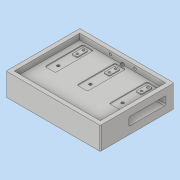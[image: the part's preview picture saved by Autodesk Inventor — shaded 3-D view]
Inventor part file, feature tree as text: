
AUTODESK INVENTOR PART (.ipt)
format: ipt  version: 2018 (Build 220112000, 112)  size: 459,264 bytes
history: native  units: mm
features: sketch x15, projected_geometry x14, extrude x8, hole x7, fillet x4, plane x1, mirror x1
ambient origin geometry x8: Origin, YZ Plane, XZ Plane, XY Plane, X Axis, Y Axis, Z Axis, Center Point
bodies: Volumenkörper1 (feature_tree)
feature tree (50):
  extrude  "Extrusion1"  Depth=180.0mm
  extrude  "Extrusion2"  Depth=10.0mm
  extrude  "Extrusion3"  Depth=27.0mm
  hole  "Bohrung1"  [1 undecoded]
  extrude  "Extrusion4"  Depth=20.0mm
  extrude  "Extrusion5"  Depth=65.5mm
  hole  "Bohrung2"  [1 undecoded]
  hole  "Bohrung3"  [1 undecoded]
  hole  "Bohrung4"  [1 undecoded]
  hole  "Bohrung5"  [1 undecoded]
  extrude  "Extrusion6"  Depth=2.0mm
  extrude  "Extrusion7"  Depth=6.5mm
  fillet  "Rundung3"  Radius=6.5mm
  plane  "Arbeitsebene1"
  mirror  "Spiegeln1"
  hole  "Bohrung6"  [1 undecoded]
  extrude  "Extrusion8"  Depth=6.5mm
  hole  "Bohrung7"  [1 undecoded]
  fillet  "Rundung2"  Radius=93.0mm
  fillet  "Rundung1"  Radius=93.0mm
  fillet  "Rundung4"  Radius=3.5mm
  sketch  "Skizze1"  dims[d0=230.0mm d1=180.0mm]
  sketch  "Skizze2"  dims[d2=39.0mm d3=0.0mm d4=10.0mm]
  projected_geometry  "Projizierte Kontur1"
  sketch  "Skizze3"  dims[d5=16.0mm d6=0.0mm d7=27.0mm]
  sketch  "Skizze4"  dims[d8=13.0mm d9=27.0mm d10=13.0mm]
  projected_geometry  "Projizierte Kontur2"
  projected_geometry  "Projizierte Kontur3"
  projected_geometry  "Projizierte Kontur4"
  projected_geometry  "Projizierte Kontur5"
  sketch  "Skizze5"  dims[d11=27.0mm d12=13.0mm d13=20.0mm]
  projected_geometry  "Projizierte Kontur6"
  sketch  "Skizze6"  dims[d14=20.0mm d15=65.5mm]
  projected_geometry  "Projizierte Kontur7"
  sketch  "Skizze7"  dims[d16=65.5mm d17=12.5mm]
  projected_geometry  "Projizierte Kontur8"
  sketch  "Skizze8"  dims[d18=2.0mm d19=0.0mm d20=15.0mm]
  projected_geometry  "Projizierte Kontur9"
  sketch  "Skizze9"  dims[d21=5.0mm]
  sketch  "Skizze10"  dims[d22=5.5mm d23=6.0mm d24=4.0mm d25=2.0mm d26=90.0deg d27=8.0mm d28=20.594885mm d29=5.0mm]
  projected_geometry  "Projizierte Kontur10"
  projected_geometry  "Projizierte Kontur11"
  projected_geometry  "Projizierte Kontur12"
  sketch  "Skizze11"  dims[d30=15.0mm d31=5.0mm]
  projected_geometry  "Projizierte Kontur13"
  sketch  "Skizze12"  dims[d32=15.0mm d33=2.0mm]
  sketch  "Skizze13"  dims[d34=6.5mm d35=6.5mm d36=6.5mm]
  sketch  "Skizze14"  dims[d37=6.5mm d38=6.5mm]
  sketch  "Skizze15"  dims[d39=6.5mm d40=6.5mm d41=93.0mm d42=93.0mm d43=93.0mm d44=93.0mm d45=3.5mm d46=20.0mm d47=10.0mm d48=0.0mm d49=9.0mm d50=9.0mm d51=9.0mm d52=9.0mm d53=9.0mm d54=9.0mm d55=5.5mm d56=0.0mm d57=6.5mm d58=2.0mm d59=14.0mm d60=10.0mm d61=6.0mm d62=4.0mm d63=2.0mm d64=90.0deg d65=12.0mm d66=20.594885mm d67=10.0mm d68=10.0mm d69=6.647mm d70=25.0mm d71=4.0mm d72=2.0mm d73=90.0deg d74=30.0mm d75=20.594885mm d76=15.0mm d77=15.0mm d78=15.0mm d79=6.647mm d80=15.0mm d81=4.0mm d82=2.0mm d83=90.0deg d84=20.0mm d85=20.594885mm d86=20.0mm d87=6.647mm d88=16.0mm d89=4.0mm d90=2.0mm d91=90.0deg d92=22.2mm d93=20.594885mm d94=20.0mm d97=10.0mm d98=0.0mm d99=90.0mm d100=20.0mm d101=20.0mm d102=70.0mm d103=18.0mm d104=17.0mm d105=25.0mm d106=0.0mm d107=3.1mm d108=-115.0mm d109=60.0mm d110=7.0mm d111=7.0mm d112=6.5mm d113=12.0mm d114=4.0mm d115=2.0mm d116=90.0deg d117=17.1mm d118=20.594885mm d119=16.0mm d120=16.0mm d121=60.0mm d122=40.0mm d123=4.0mm d124=0.0mm d125=60.0mm d126=7.0mm d127=6.5mm d128=12.0mm d129=4.0mm d130=2.0mm d131=90.0deg d132=17.1mm d133=20.594885mm d134=3.1mm]
  projected_geometry  "Projizierte Kontur14"
note: 7 required parameter values undecoded (feature->parameter linkage not recoverable at this tier; creation-order binding heuristic only, values carry confidence <= 0.55)
